# Revit family: AFX-Cass-Led_Flush_Mount-1
name_source: partatom
category: Lighting Fixtures
units: mm (PartAtom-declared; Revit-internal decimal feet)

## family parameters
Cut with Voids When Loaded = No
Host = Face
Light Source = Yes
Part Type = Normal
Room Calculation Point = No
Round Connector Dimension = Use Diameter
Shared = No

## types (2) — shared parameters
Apparent Load = 0 VA
Assembly Code = D5020200
Canopy Finish = AFX - Aluminum Black
Color Filter = 16777215
Colour Rendering Index = 90
Cord Finish = AFX - Plastic Black
Default Elevation = 48"
Diffuser Finish = AFX - White Acrylic
Dimming Lamp Color Temperature Shift = <None>
Emit Shape Visible in Rendering = No
Emit from Circle Diameter = 24"
Frame Finish = AFX - Aluminum Black
Height = 5 1/4"
Keynote = 12500
Manufacturer = AFX Inc
Product Documentation Link = https://www.afxinc.com
Support Finish = AFX - Aluminum Black
Tilt Angle = -90.00°
Type Comments = Cass
URL = https://www.afxinc.com
Voltage = 120 V

## per-type parameters (varying)
| type | Description | Diameter | Dist Ies | Photometric Web File | Wattage Comments |
| CSSC13L30D1BK | Contemporary LED flush mount with three sided illumination White acrylic diffuser - 13"Diameter x 5 1/4"H | 13" | 8" | CSSC13L30D1xx_IES.IES | 30W |
| CSSC17L30D1BK | Contemporary LED flush mount with three sided illumination White acrylic diffuser - 17"Diameter x 5 1/4"H | 17" | 10" | CSSC17L30D1XX.IES | 38W |

note: column(s) folded — value = type name in every type: Model

## geometry (parser evidence)
native form markers: Sweep x6
no freeform markers — native parametric forms only
